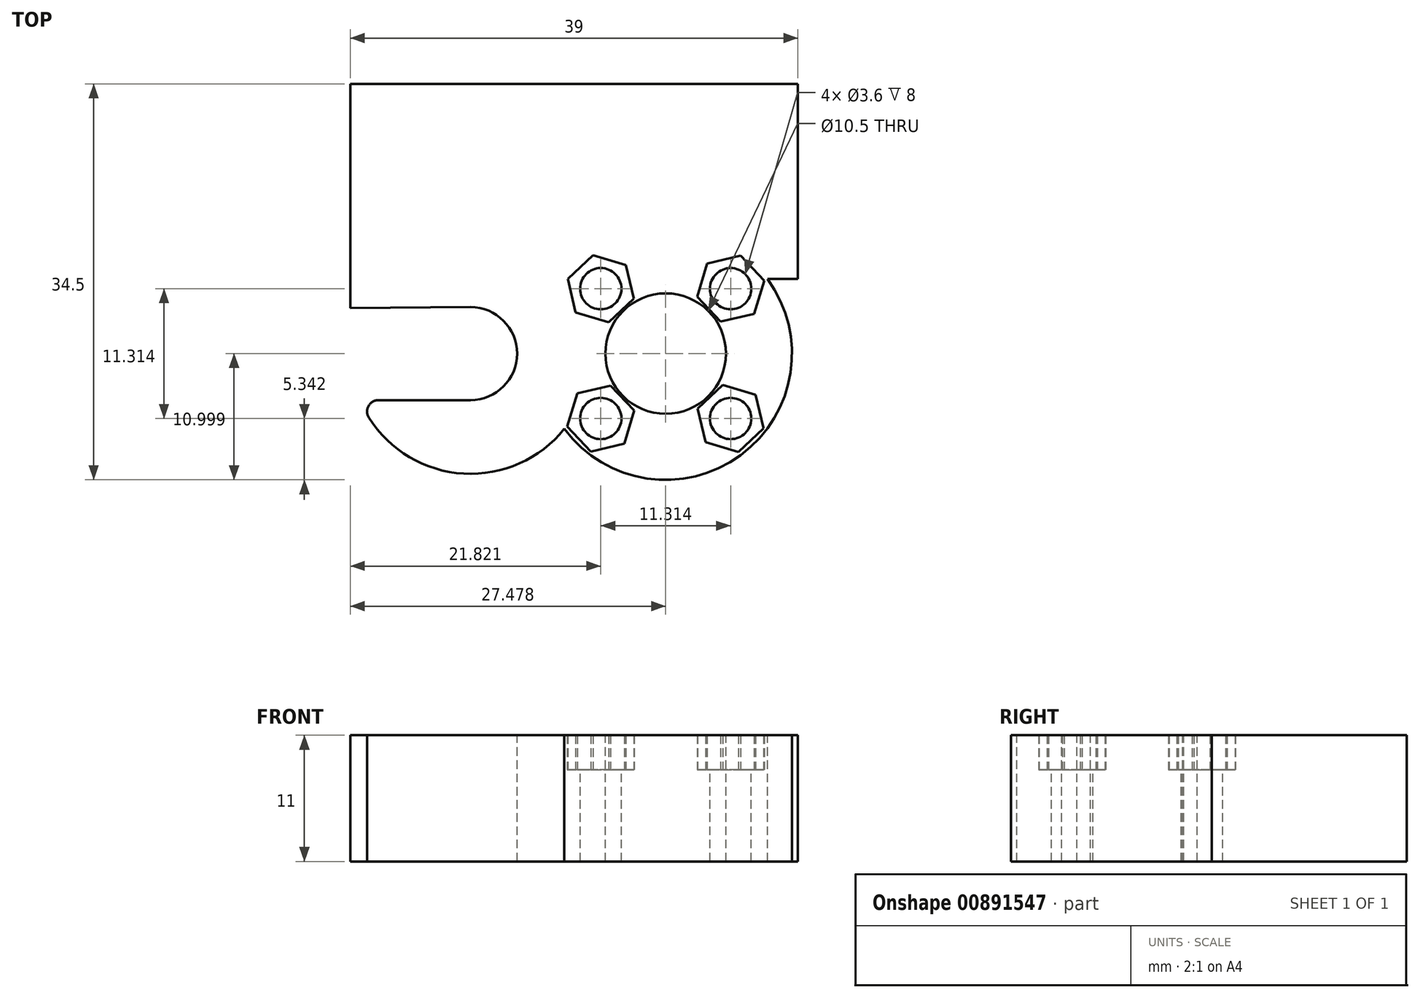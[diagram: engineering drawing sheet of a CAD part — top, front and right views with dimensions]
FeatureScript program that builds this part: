
annotation { "Feature Type Name" : "Feature", "Feature Type Description" : "" }
export const myFeature = defineFeature(function(context is Context, id is Id, definition is map)
    precondition{}
    {
        {
            var Q0;
            Q0=qCreatedBy(makeId("Top.planeOp"),FACE);
            var sketch = newSketch(context, id + "F0", { "sketchPlane" : qUnion([Q0])});
            skLineSegment(sketch, "E0", {"start": v(48.58, 7.87) * mm, "end": v(-76.76, 7.87) * mm, "construction": true});
            skPoint(sketch, "E0.startSnap0", {"position": v(26.1, 7.87) * mm});
            skLineSegment(sketch, "E1", {"start": v(-2.4, 49.8) * mm, "end": v(-2.4, -30.5) * mm, "construction": true});
            skLineSegment(sketch, "E2", {"start": v(-12.88, 19.54) * mm, "end": v(26.12, 19.54) * mm});
            skLineSegment(sketch, "E3", {"start": v(26.12, 19.54) * mm, "end": v(26.12, 2.54) * mm});
            skLineSegment(sketch, "E4", {"start": v(26.12, 2.54) * mm, "end": v(23.47, 2.54) * mm});
            skLineSegment(sketch, "E5", {"start": v(-2.4, -3.96) * mm, "end": v(31.93, -3.96) * mm, "construction": true});
            skPoint(sketch, "E6.end.orphan", {"position": v(8.07, 2.54) * mm});
            skCircle(sketch, "E7", {"center": v(14.6, -3.96) * mm, "radius": 5.25 * mm});
            skCircle(sketch, "E8", {"center": v(14.6, -3.96) * mm, "radius": 8 * mm, "construction": true});
            skArc(sketch, "E9", {"start": v(-2.4, -8.01) * mm, "mid": v(1.65, -3.96) * mm, "end": v(-2.4, 0.09) * mm});
            skLineSegment(sketch, "E10", {"start": v(-2.4, -8.01) * mm, "end": v(-10.42, -8.01) * mm});
            skArc(sketch, "E11.filletArc", {"start": v(-10.42, -8.01) * mm, "mid": v(-11.3, -8.53) * mm, "end": v(-11.27, -9.54) * mm});
            skLineSegment(sketch, "E12", {"start": v(14.6, -3.96) * mm, "end": v(22.2, 3.63) * mm, "construction": true});
            skCircle(sketch, "E13", {"center": v(20.25, 1.7) * mm, "radius": 1.8 * mm});
            skCircle(sketch, "E14.1.0", {"center": v(8.94, 1.7) * mm, "radius": 1.8 * mm});
            skCircle(sketch, "E14.2.0", {"center": v(8.94, -9.62) * mm, "radius": 1.8 * mm});
            skCircle(sketch, "E14.3.0", {"center": v(20.25, -9.62) * mm, "radius": 1.8 * mm});
            skLineSegment(sketch, "E15", {"start": v(-2.4, 0.09) * mm, "end": v(-12.88, 0) * mm});
            skLineSegment(sketch, "E16", {"start": v(-12.88, 0) * mm, "end": v(-12.88, 19.54) * mm});
            skArc(sketch, "E17", {"start": v(5.77, -10.52) * mm, "mid": v(21.13, -12.81) * mm, "end": v(23.47, 2.54) * mm});
            skArc(sketch, "E18", {"start": v(-11.27, -9.54) * mm, "mid": v(-3, -14.42) * mm, "end": v(5.77, -10.52) * mm});
            skSolve(sketch);
        }
        {
            var Q0;
            Q0=makeQuery(id+"F0.imprint","IMPRINT",FACE,{"disambiguationData":[TD([[makeQuery(id+"F0.imprint","IMPRINT",EDGE,{"derivedFrom":sQuery(id+"F0.wireOp",EDGE,"E2")}),-1.0]])]});
            extrude(context, id + "F1", {"entities" : qUnion([Q0]), "oppositeDirection" : true, "depth" : 8 * mm, "offsetDistance" : 25 * mm});
        }
        {
            var Q0;
            Q0=makeQuery(id+"F1.opExtrude","CAP_FACE",FACE,{"disambiguationData":[OSD([sQuery(id+"F0.wireOp",EDGE,"971d9a5d-a778-4eb9-8f99-298300e5a9f5"),sQuery(id+"F0.wireOp",EDGE,"E2"),sQuery(id+"F0.wireOp",EDGE,"E3"),sQuery(id+"F0.wireOp",EDGE,"E4"),sQuery(id+"F0.wireOp",EDGE,"0vNkUIAS-u63n-jiYH-kE6m-wjBRh7Gk0M3G"),sQuery(id+"F0.wireOp",EDGE,"kDs3BF4U-yivp-poZi-H3ak-LXh5FsVPtUeV"),sQuery(id+"F0.wireOp",EDGE,"E7"),sQuery(id+"F0.wireOp",EDGE,"E9"),sQuery(id+"F0.wireOp",EDGE,"E10"),sQuery(id+"F0.wireOp",EDGE,"MkTmpDUm-10Gx-Ubqo-38nI-D6oixlnNXrtN"),sQuery(id+"F0.wireOp",EDGE,"E11.filletArc"),sQuery(id+"F0.wireOp",EDGE,"ab16ec52-eb72-4a04-bab6-42f2a6c3ff08.filletArc"),sQuery(id+"F0.wireOp",EDGE,"c936695a-1612-4784-b77d-c9354304d2ff.filletArc"),sQuery(id+"F0.wireOp",EDGE,"E13"),sQuery(id+"F0.wireOp",EDGE,"E14.1.0"),sQuery(id+"F0.wireOp",EDGE,"E14.2.0"),sQuery(id+"F0.wireOp",EDGE,"E14.3.0")])],"isStart":true});
            var sketch = newSketch(context, id + "F2", { "sketchPlane" : qUnion([Q0])});
            skCircle(sketch, "E19.cCircle", {"center": v(20.25, -9.62) * mm, "radius": 2.6 * mm, "construction": true});
            skLineSegment(sketch, "E19.0", {"start": v(22.44, -7.56) * mm, "end": v(23.13, -10.48) * mm});
            skLineSegment(sketch, "E19.1", {"start": v(23.13, -10.48) * mm, "end": v(20.94, -12.54) * mm});
            skLineSegment(sketch, "E19.2", {"start": v(20.94, -12.54) * mm, "end": v(18.07, -11.68) * mm});
            skLineSegment(sketch, "E19.3", {"start": v(18.07, -11.68) * mm, "end": v(17.38, -8.76) * mm});
            skLineSegment(sketch, "E19.4", {"start": v(17.38, -8.76) * mm, "end": v(19.57, -6.7) * mm});
            skLineSegment(sketch, "E19.5", {"start": v(19.57, -6.7) * mm, "end": v(22.44, -7.56) * mm});
            skPoint(sketch, "E19.0.midPoint", {"position": v(22.78, -9.02) * mm});
            skPoint(sketch, "E20.1.0", {"position": v(19.66, 4.22) * mm});
            skCircle(sketch, "E20.1.1", {"center": v(20.25, 1.7) * mm, "radius": 2.6 * mm, "construction": true});
            skLineSegment(sketch, "E20.1.2", {"start": v(21.12, 4.57) * mm, "end": v(23.17, 2.38) * mm});
            skLineSegment(sketch, "E20.1.3", {"start": v(23.17, 2.38) * mm, "end": v(22.31, -0.49) * mm});
            skLineSegment(sketch, "E20.1.4", {"start": v(22.31, -0.49) * mm, "end": v(19.4, -1.18) * mm});
            skLineSegment(sketch, "E20.1.5", {"start": v(19.4, -1.18) * mm, "end": v(17.34, 1) * mm});
            skLineSegment(sketch, "E20.1.6", {"start": v(18.2, 3.88) * mm, "end": v(21.12, 4.57) * mm});
            skLineSegment(sketch, "E20.1.7", {"start": v(17.34, 1) * mm, "end": v(18.2, 3.88) * mm});
            skPoint(sketch, "E20.2.0", {"position": v(6.41, 1.1) * mm});
            skCircle(sketch, "E20.2.1", {"center": v(8.94, 1.7) * mm, "radius": 2.6 * mm, "construction": true});
            skLineSegment(sketch, "E20.2.2", {"start": v(6.07, 2.56) * mm, "end": v(8.25, 4.62) * mm});
            skLineSegment(sketch, "E20.2.3", {"start": v(8.25, 4.62) * mm, "end": v(11.13, 3.75) * mm});
            skLineSegment(sketch, "E20.2.4", {"start": v(11.13, 3.75) * mm, "end": v(11.81, 0.83) * mm});
            skLineSegment(sketch, "E20.2.5", {"start": v(11.81, 0.83) * mm, "end": v(9.63, -1.22) * mm});
            skLineSegment(sketch, "E20.2.6", {"start": v(6.76, -0.36) * mm, "end": v(6.07, 2.56) * mm});
            skLineSegment(sketch, "E20.2.7", {"start": v(9.63, -1.22) * mm, "end": v(6.76, -0.36) * mm});
            skPoint(sketch, "E20.3.0", {"position": v(9.54, -12.15) * mm});
            skCircle(sketch, "E20.3.1", {"center": v(8.94, -9.62) * mm, "radius": 2.6 * mm, "construction": true});
            skLineSegment(sketch, "E20.3.2", {"start": v(8.08, -12.5) * mm, "end": v(6.02, -10.3) * mm});
            skLineSegment(sketch, "E20.3.3", {"start": v(6.02, -10.3) * mm, "end": v(6.88, -7.43) * mm});
            skLineSegment(sketch, "E20.3.4", {"start": v(6.88, -7.43) * mm, "end": v(9.8, -6.75) * mm});
            skLineSegment(sketch, "E20.3.5", {"start": v(9.8, -6.75) * mm, "end": v(11.86, -8.93) * mm});
            skLineSegment(sketch, "E20.3.6", {"start": v(11, -11.8) * mm, "end": v(8.08, -12.5) * mm});
            skLineSegment(sketch, "E20.3.7", {"start": v(11.86, -8.93) * mm, "end": v(11, -11.8) * mm});
            skPoint(sketch, "E20.center", {"position": v(14.6, -3.96) * mm});
            skSolve(sketch);
        }
        {
            var Q0;
            Q0=makeQuery(id+"F2.imprint","IMPRINT",FACE,{"disambiguationData":[TD([[makeQuery(id+"F2.imprint","IMPRINT",EDGE,{"derivedFrom":sQuery(id+"F2.wireOp",EDGE,"E19.0")}),1.0]])]});
            extrude(context, id + "F3", {"entities" : qUnion([Q0]), "operationType" : NewBodyOperationType.ADD, "depth" : 3 * mm, "offsetDistance" : 25 * mm});
        }
    });
